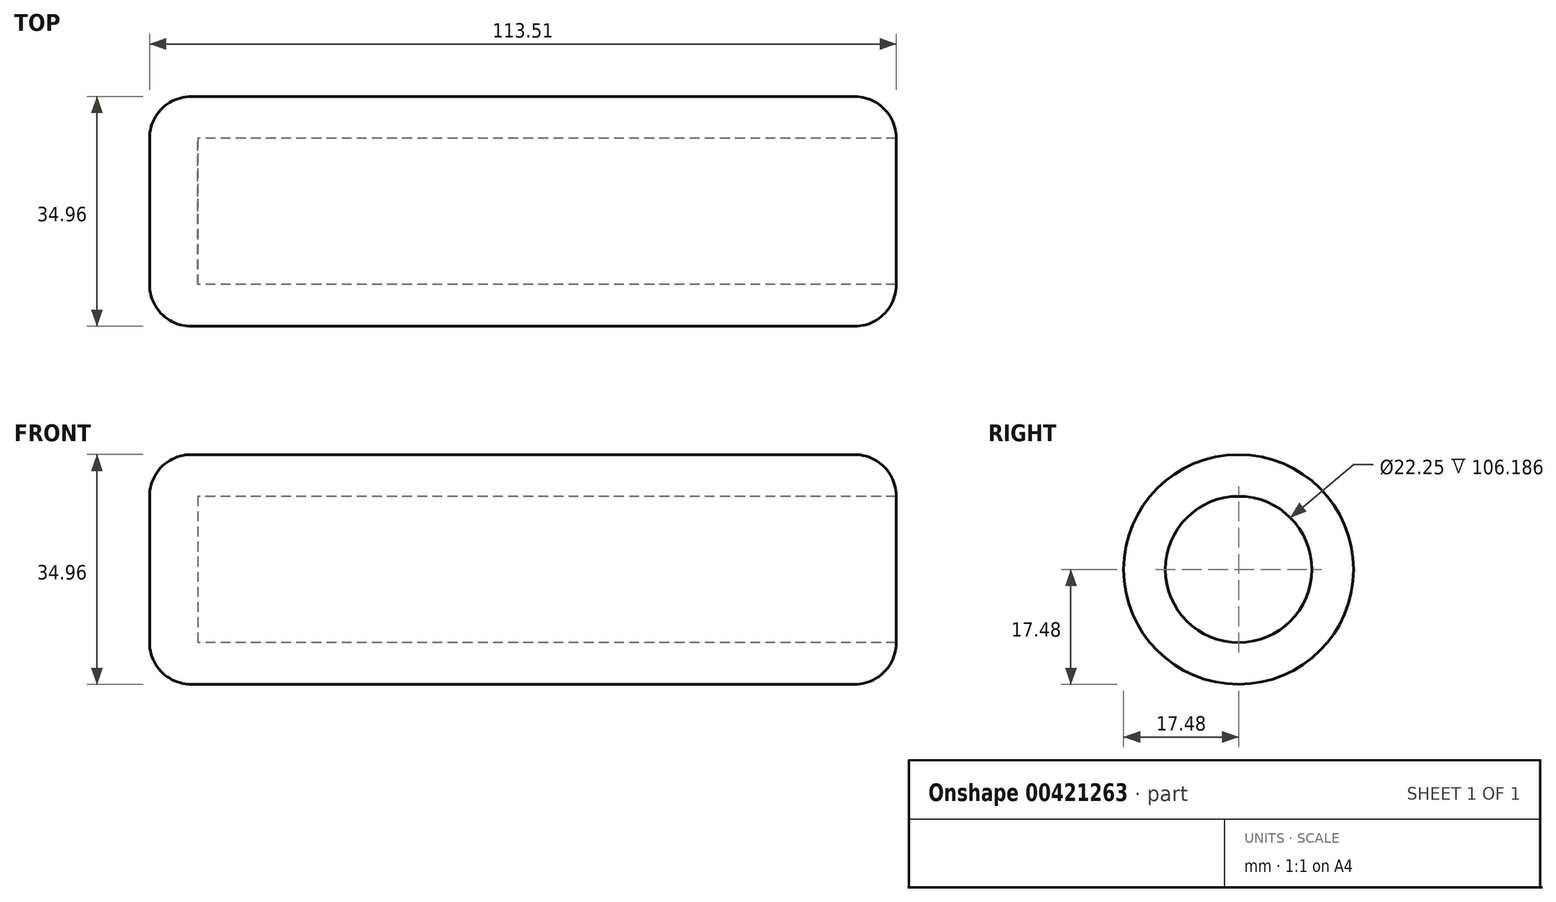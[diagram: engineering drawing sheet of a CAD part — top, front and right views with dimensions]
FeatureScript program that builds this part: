
annotation { "Feature Type Name" : "Feature", "Feature Type Description" : "" }
export const myFeature = defineFeature(function(context is Context, id is Id, definition is map)
    precondition{}
    {
        {
            var Q0;
            Q0=qCreatedBy(makeId("Front.planeOp"),FACE);
            var sketch = newSketch(context, id + "F0", { "sketchPlane" : qUnion([Q0])});
            skLineSegment(sketch, "E0", {"start": v(0, 0) * mm, "end": v(0, -17.48) * mm});
            skLineSegment(sketch, "E1", {"start": v(0, -17.48) * mm, "end": v(113.51, -17.48) * mm});
            skLineSegment(sketch, "E2", {"start": v(113.51, -17.48) * mm, "end": v(113.51, -11.13) * mm});
            skLineSegment(sketch, "E3", {"start": v(113.51, -11.13) * mm, "end": v(7.33, -11.13) * mm});
            skLineSegment(sketch, "E4", {"start": v(7.33, -11.13) * mm, "end": v(7.33, 0) * mm});
            skLineSegment(sketch, "E5", {"start": v(7.33, 0) * mm, "end": v(0, 0) * mm});
            skLineSegment(sketch, "E6", {"start": v(-23.49, 0) * mm, "end": v(60.68, 0) * mm, "construction": true});
            skSolve(sketch);
        }
        {
            var Q0;
            Q0=makeQuery(id+"F0.imprint","IMPRINT",FACE,{"disambiguationData":[TD([[makeQuery(id+"F0.imprint","IMPRINT",EDGE,{"derivedFrom":sQuery(id+"F0.wireOp",EDGE,"E0")}),1.0]])]});
            var Q1;
            Q1=sQuery(id+"F0.wireOp",EDGE,"E6");
            revolve(context, id + "F1", {"entities" : qUnion([Q0]), "axis" : qUnion([Q1]), "revolveType" : RevolveType.FULL});
        }
        {
            var Q0;
            Q0=makeQuery(id+"F1.opRevolve","SWEPT_FACE",FACE,{"disambiguationData":[OSD([sQuery(id+"F0.wireOp",EDGE,"E0")])]});
            var Q1;
            Q1=makeQuery(id+"F1.opRevolve","SWEPT_EDGE",EDGE,{"disambiguationData":[OSD([sQuery(id+"F0.wireOp",EDGE,"E1"),sQuery(id+"F0.wireOp",EDGE,"E2")])]});
            fillet(context, id + "F2", {"entities" : qUnion([Q0, Q1]), "radius" : 6.35 * mm, "tangentPropagation" : true, "allowEdgeOverflow" : false});
        }
    });
